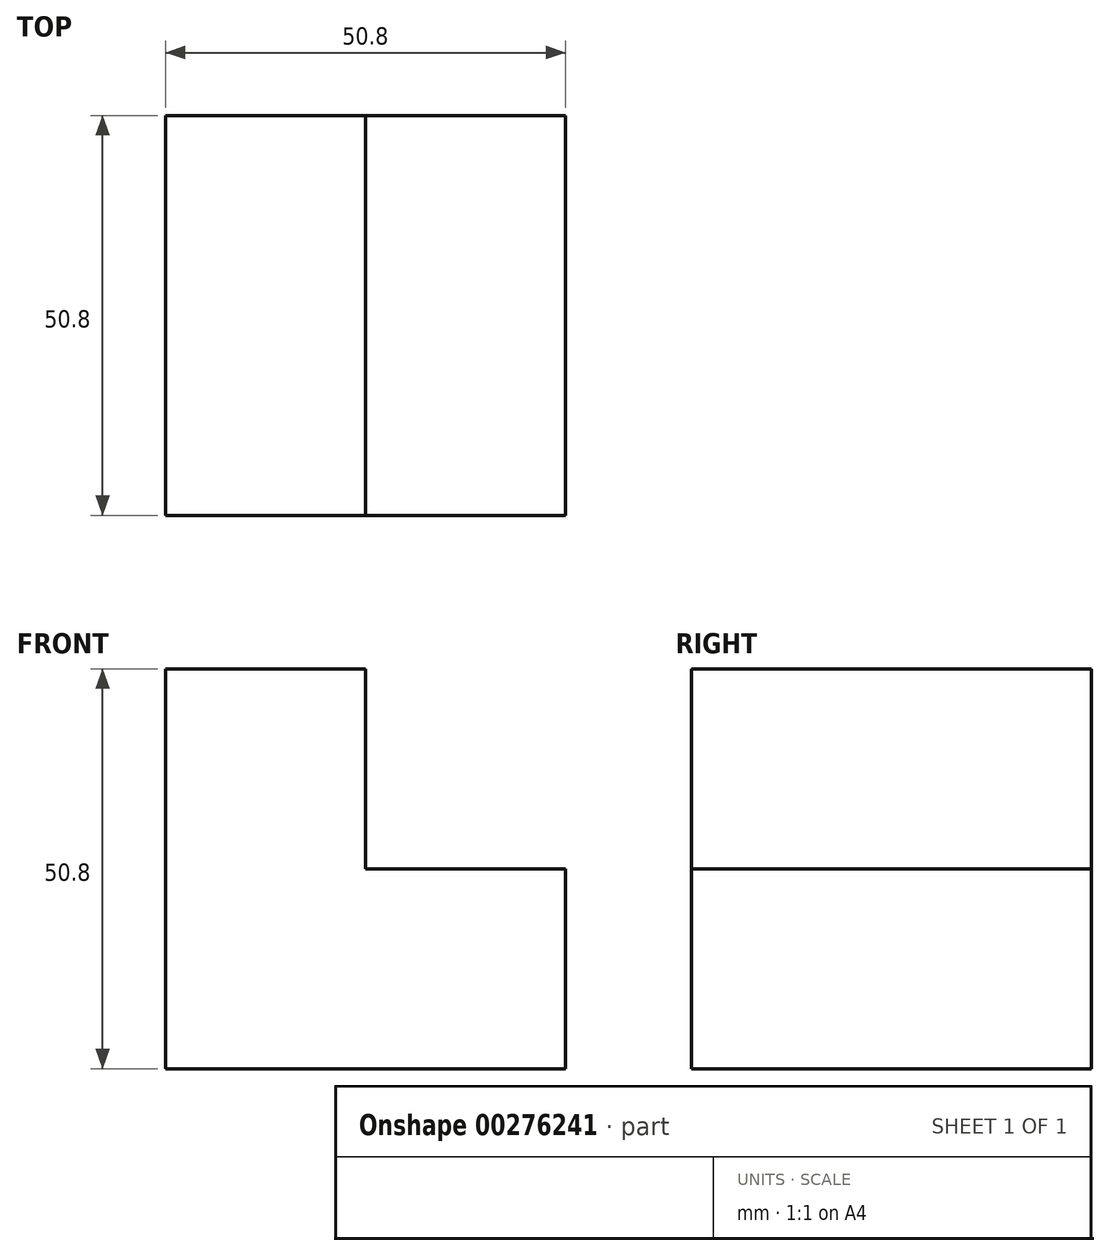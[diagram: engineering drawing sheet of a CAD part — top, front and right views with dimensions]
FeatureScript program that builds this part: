
annotation { "Feature Type Name" : "Feature", "Feature Type Description" : "" }
export const myFeature = defineFeature(function(context is Context, id is Id, definition is map)
    precondition{}
    {
        {
            var Q0;
            Q0=qCreatedBy(makeId("Front.planeOp"),FACE);
            var sketch = newSketch(context, id + "F0", { "sketchPlane" : qUnion([Q0])});
            skLineSegment(sketch, "E0", {"start": v(-41.67, 75.5) * mm, "end": v(-41.67, 24.7) * mm});
            skLineSegment(sketch, "E1", {"start": v(-41.67, 24.7) * mm, "end": v(9.13, 24.7) * mm});
            skLineSegment(sketch, "E2", {"start": v(9.13, 24.7) * mm, "end": v(9.13, 50.1) * mm});
            skLineSegment(sketch, "E3", {"start": v(9.13, 50.1) * mm, "end": v(-16.27, 50.1) * mm});
            skLineSegment(sketch, "E4", {"start": v(-16.27, 50.1) * mm, "end": v(-16.27, 75.5) * mm});
            skLineSegment(sketch, "E5", {"start": v(-16.27, 75.5) * mm, "end": v(-41.67, 75.5) * mm});
            skSolve(sketch);
        }
        {
            var Q0;
            Q0 = qSketchRegion(id + "F0", true);
            extrude(context, id + "F1", {"entities" : qUnion([Q0]), "depth" : 50.8 * mm});
        }
    });
